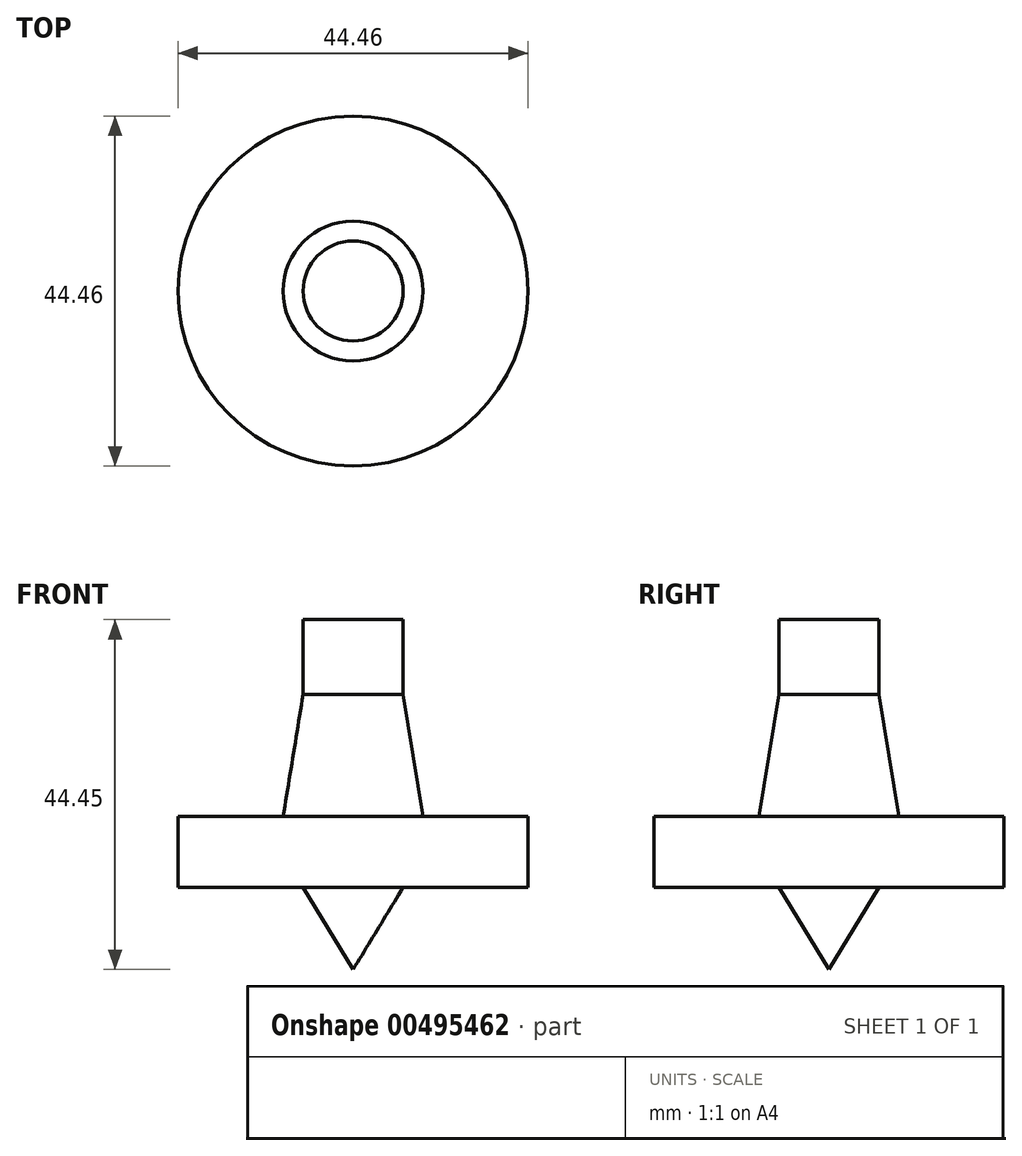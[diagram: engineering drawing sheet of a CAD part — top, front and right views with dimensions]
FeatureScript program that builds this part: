
annotation { "Feature Type Name" : "Feature", "Feature Type Description" : "" }
export const myFeature = defineFeature(function(context is Context, id is Id, definition is map)
    precondition{}
    {
        {
            var Q0;
            Q0=qCreatedBy(makeId("Front.planeOp"),FACE);
            var sketch = newSketch(context, id + "F0", { "sketchPlane" : qUnion([Q0])});
            skLineSegment(sketch, "E0", {"start": v(6.35, 34.05) * mm, "end": v(6.35, 24.53) * mm});
            skLineSegment(sketch, "E1", {"start": v(6.35, 0) * mm, "end": v(0, -10.4) * mm});
            skLineSegment(sketch, "E2.MirrorCS", {"start": v(-6.35, 0) * mm, "end": v(0, -10.4) * mm});
            skLineSegment(sketch, "E3.MirrorCS", {"start": v(-6.35, 34.05) * mm, "end": v(-6.35, 24.53) * mm});
            skLineSegment(sketch, "E4", {"start": v(6.35, 0) * mm, "end": v(22.23, 0) * mm});
            skLineSegment(sketch, "E5", {"start": v(22.23, 0) * mm, "end": v(22.23, 9.01) * mm});
            skLineSegment(sketch, "E6", {"start": v(22.23, 9.01) * mm, "end": v(8.89, 9.01) * mm});
            skLineSegment(sketch, "E7.MirrorCS", {"start": v(-22.23, 9.01) * mm, "end": v(-8.9, 9.01) * mm});
            skLineSegment(sketch, "E8.MirrorCS", {"start": v(-22.23, 0) * mm, "end": v(-22.23, 9.01) * mm});
            skLineSegment(sketch, "E9.MirrorCS", {"start": v(-6.35, 0) * mm, "end": v(-22.23, 0) * mm});
            skLineSegment(sketch, "E10", {"start": v(6.35, 24.53) * mm, "end": v(8.89, 9.01) * mm});
            skLineSegment(sketch, "E11", {"start": v(-6.35, 24.53) * mm, "end": v(-8.9, 9.01) * mm});
            skLineSegment(sketch, "E12", {"start": v(-6.35, 34.05) * mm, "end": v(6.35, 34.05) * mm});
            skLineSegment(sketch, "E13", {"start": v(0, -10.4) * mm, "end": v(0, 34.05) * mm});
            skSolve(sketch);
        }
        {
            var Q0;
            {var subQ0=sQuery(id+"F0.wireOp",EDGE,"E0");Q0=makeQuery(id+"F0.imprint","IMPRINT",FACE,{"disambiguationData":[TD([[makeQuery(id+"F0.imprint","IMPRINT",EDGE,{"derivedFrom":subQ0}),-1.0]])]});}
            var Q1;
            Q1=sQuery(id+"F0.wireOp",EDGE,"E13");
            revolve(context, id + "F1", {"entities" : qUnion([Q0]), "axis" : qUnion([Q1]), "revolveType" : RevolveType.FULL});
        }
    });
